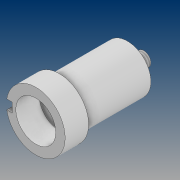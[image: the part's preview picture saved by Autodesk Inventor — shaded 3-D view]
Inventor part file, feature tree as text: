
AUTODESK INVENTOR PART (.ipt)
format: ipt  version: 2021 (Build 250183000, 183)  size: 142,336 bytes
history: native  units: mm
features: extrude x6, sketch x5, thread x1
ambient origin geometry x8: Origin, YZ Plane, XZ Plane, XY Plane, X Axis, Y Axis, Z Axis, Center Point
bodies: Solid1 (feature_tree)
feature tree (12):
  sketch  "Sketch1"  dims[d0=0.0mm d1=0.0mm]
  extrude  "Extrusion1"  TaperAngle=0.0deg  [1 undecoded]
  extrude  "Extrusion2"  TaperAngle=0.0deg  [1 undecoded]
  extrude  "Extrusion3"  Depth=20.0mm
  extrude  "Extrusion4"  Depth=29.0mm TaperAngle=0.0deg
  thread  "Thread1"  [1 undecoded]
  extrude  "Extrusion5"  Depth=6.0mm
  extrude  "Extrusion6"  Depth=6.0mm TaperAngle=0.0deg
  sketch  "Sketch2"  dims[d2=0.0mm d3=0.0mm]
  sketch  "Sketch3"  dims[d4=25.0mm d5=20.0mm]
  sketch  "Sketch4"  dims[d6=10.0mm d7=0.0mm d8=29.0mm d9=0.0mm d10=17.0mm]
  sketch  "Sketch5"  dims[d11=1.0mm d12=0.0mm d13=6.0mm d14=6.0mm d15=0.0mm d16=6.0mm d17=0.0mm d18=0.0mm d19=0.0mm d20=10.0mm d21=0.0mm]
note: 3 required parameter values undecoded (feature->parameter linkage not recoverable at this tier; creation-order binding heuristic only, values carry confidence <= 0.55)
